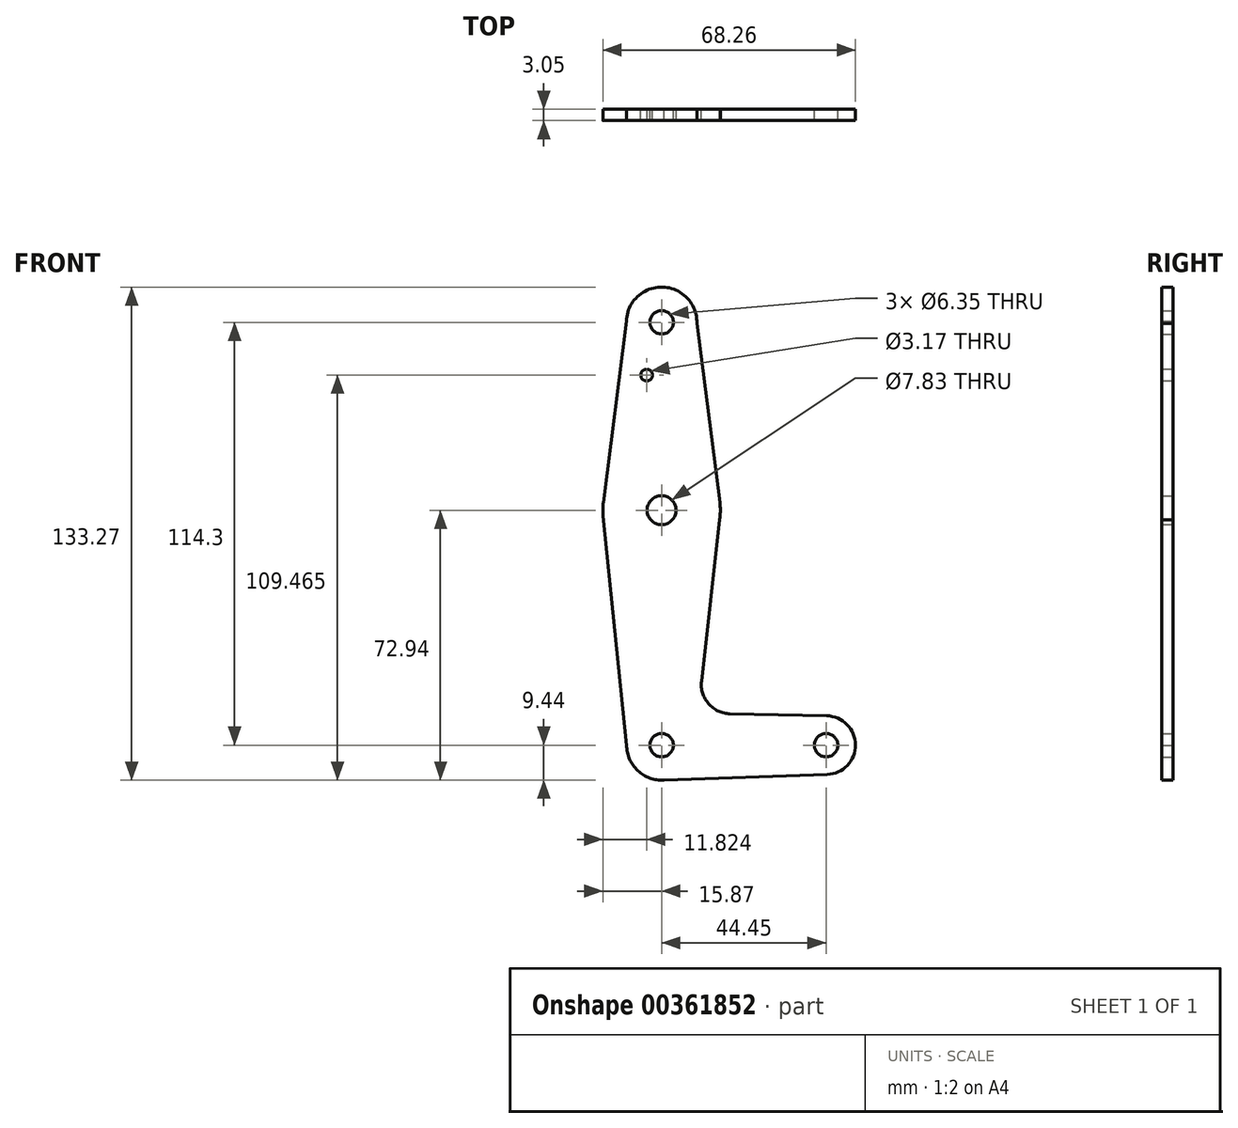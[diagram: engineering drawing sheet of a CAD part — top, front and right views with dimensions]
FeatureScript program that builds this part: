
annotation { "Feature Type Name" : "Feature", "Feature Type Description" : "" }
export const myFeature = defineFeature(function(context is Context, id is Id, definition is map)
    precondition{}
    {
        {
            var Q0;
            Q0=qCreatedBy(makeId("Front.planeOp"),FACE);
            var sketch = newSketch(context, id + "F0", { "sketchPlane" : qUnion([Q0])});
            skLineSegment(sketch, "E0", {"start": v(0, 0) * mm, "end": v(0, 114.3) * mm, "construction": true});
            skLineSegment(sketch, "E1", {"start": v(0, 0) * mm, "end": v(44.45, 0) * mm, "construction": true});
            skCircle(sketch, "E2", {"center": v(0, 0) * mm, "radius": 9.44 * mm});
            skCircle(sketch, "E3", {"center": v(44.45, 0) * mm, "radius": 7.94 * mm});
            skCircle(sketch, "E4", {"center": v(0, 114.3) * mm, "radius": 9.53 * mm});
            skPoint(sketch, "E5", {"position": v(0, 63.5) * mm});
            skCircle(sketch, "E6", {"center": v(0, 63.5) * mm, "radius": 15.88 * mm});
            skLineSegment(sketch, "E7", {"start": v(-15.76, 65.44) * mm, "end": v(-9.29, 116.42) * mm});
            skLineSegment(sketch, "E8", {"start": v(15.76, 65.44) * mm, "end": v(9.13, 117.01) * mm});
            skLineSegment(sketch, "E9", {"start": v(15.85, 62.62) * mm, "end": v(10.78, 17.3) * mm});
            skLineSegment(sketch, "E10", {"start": v(18.52, 8.47) * mm, "end": v(44.61, 7.94) * mm});
            skLineSegment(sketch, "E11", {"start": v(0, -9.44) * mm, "end": v(44.72, -7.93) * mm});
            skCircle(sketch, "E12", {"center": v(0, 114.3) * mm, "radius": 3.18 * mm});
            skCircle(sketch, "E13", {"center": v(0, 63.5) * mm, "radius": 3.92 * mm});
            skCircle(sketch, "E14", {"center": v(44.45, 0) * mm, "radius": 3.18 * mm});
            skArc(sketch, "E15.filletArc", {"start": v(10.78, 17.3) * mm, "mid": v(12.7, 11.18) * mm, "end": v(18.52, 8.47) * mm});
            skCircle(sketch, "E16", {"center": v(-4.05, 100.03) * mm, "radius": 1.59 * mm});
            skLineSegment(sketch, "E17", {"start": v(-9.44, 0) * mm, "end": v(-15.8, 61.9) * mm});
            skCircle(sketch, "E18", {"center": v(0, 0) * mm, "radius": 3.18 * mm});
            skSolve(sketch);
        }
        {
            var Q0;
            Q0 = qSketchRegion(id + "F0", true);
            var Q1;
            {var subQ0=sQuery(id+"F0.wireOp",EDGE,"E18");var subQ1=sQuery(id+"F0.wireOp",EDGE,"E0");var subQ2=makeQuery(id+"F0.imprint","INTERSECT",VERTEX,{"derivedFrom":[subQ1,subQ0]});Q1=makeQuery(id+"F0.imprint","IMPRINT",FACE,{"disambiguationData":[TD([[makeQuery(id+"F0.imprint","IMPRINT",EDGE,{"disambiguationData":[TD([[subQ2,-1.0]])],"derivedFrom":subQ1}),-1.0]])]});}
            extrude(context, id + "F1", {"entities" : qUnion([Q0, Q1]), "depth" : 3.05 * mm});
        }
    });
